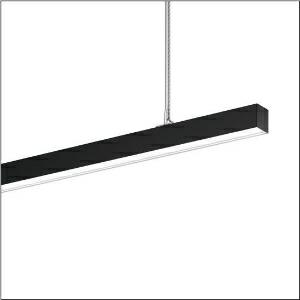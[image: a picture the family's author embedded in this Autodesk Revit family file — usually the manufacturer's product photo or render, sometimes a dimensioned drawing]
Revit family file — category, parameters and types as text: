
# Revit family: silica_21_51mx33tat7b
name_source: partatom
category: Lighting Fixtures
units: mm (PartAtom-declared; Revit-internal decimal feet)

## family parameters
Cut with Voids When Loaded = No
Host = Face
Light Source = No
Part Type = Normal
Room Calculation Point = No
Round Connector Dimension = Use Diameter
Shared = No

## types (1)
- --- (1 x LED, 5740 lm, 53.8 W, 6500K)
    Apparent Load = 54 VA
    CIE Flux Codes = 78 96 99 56 100
    Color Rendering = 80
    Color Temperature = 6500K
    Default Elevation = 1800 mm
    Description = Silica 21, office luminaire, primary optical cover: prismatic diffuser, of PMMA, CAT 2 (L<= 3000cd/m²), light emission: direct/indirect distribution, primary light characteristic: symmetric, installation type: suspended mounting, LED, rated luminous flux: 5.740lm, luminous efficacy: 102lm/W, light colour: 8tw, colour temperature: 2700..6500K, control gear: DALI DT8, with terminal, 3+2-pole, max. 2.5mm², mains connection: 220..240V, AC, 50/60Hz, rated input power: 56.5W, luminaire housing, of aluminium, matt jet black (RAL 9005), length: 1.204mm, width: 53mm, height: 53mm, protection rating (complete): IP20, insulation class (complete): insulation class I (protective earthing), certification: CE, permissible operating ambient temperature: 0..+35°C, standard: EN 50419, packaging unit: 1 piece
    Height = 53 mm
    Lamp = 1 x LED
    Lamp Light Flux = 5740 lm
    Lamp Power = 53.8 W
    Lamp count = 1
    Length = 1204 mm
    Luminous efficacy = 107 lm/W
    Manufacturer = Siteco
    ModVariant = No
    Model = 51MX33TAT7B
    Mounting Place = Ceiling
    Mounting Type = Pendant
    Number of Poles = 1
    OnlyDefault = Yes
    Power Factor = 1
    Product Name = Silica 21
    Product group = office luminaire | ceiling pendant
    ProductGroupID = 903
    Protection Class = Protection class I
    Protection Degree = IP 20
    RLX_Detail_Level = 1
    RLX_Emergency_Light_Flux = 0 lm
    RLX_Emergency_Type = 0
    RLX_Emergency_Type_DB = No
    RlxData = <blob elided: 22881 chars, md5=3a4178b2>
    Socket = socket
    Standby Power = 0 W
    System Light Flux = 5740 lm
    System Power = 54 W
    Type Comments = individual setting
    Type Image = l_1335856.jpg
    URL = http://relux.com
    VarID = @adj_139259
    Voltage = 0 V
    Weight = 0.00 kg
    Width = 53 mm

## geometry (parser evidence)
native form markers: Blend x4, Sweep x13
no freeform markers — native parametric forms only
